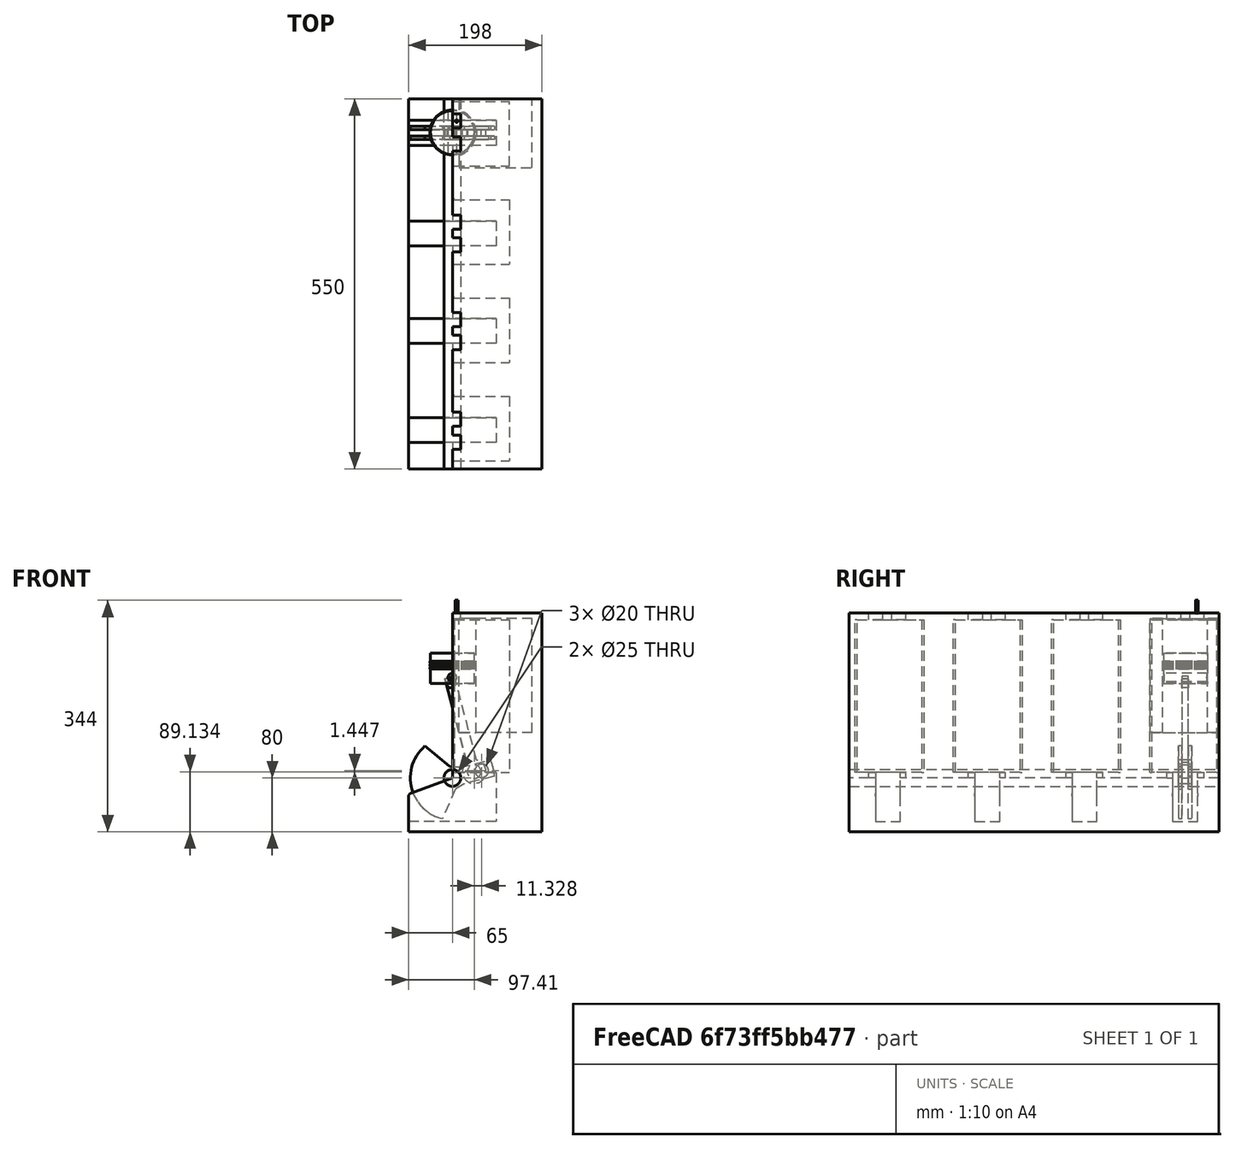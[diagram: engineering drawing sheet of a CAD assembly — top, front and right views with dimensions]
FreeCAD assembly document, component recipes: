
FREECAD ASSEMBLY — COMPONENT RECIPES ("motor")

This assembly document has 7 components, labeled P0..P6 below (a component is one placed body or linked part). 7 of them carry a construction recipe — the FreeCAD feature program that regenerates the part from scratch, quoted from this document or its linked companion documents; the rest are supplied as boundary geometry only. No exploded tour is included for this assembly.
COMPONENT P0 — recipe-attached ("Body", modeled in this document).
Construction recipe (the document's own serialized feature program — sketch geometry with constraints, then the solid features built on it; lengths are millimeters unless a unit is written):

FEATURE [Sketcher::SketchObject] Sketch
  ArcFitTolerance = 1e-06
  AttachmentSupport = -> [XZ_Plane]
  FullyConstrained = true
  MakeInternals = false
  MapMode = 5
  Placement = pos=(0,0,0) rot=(1,0,0;1.5708rad)
  sketch-geometry (1):
    g0: Circle CenterX=0 CenterY=0 CenterZ=0 NormalX=0 NormalY=0 NormalZ=1 AngleXU=0 Radius=12.5
  constraints (2):
    c: Diameter(g0) = 25
    c: Coincident(g0,g-1)
FEATURE [PartDesign::Pad] Pad
  Direction = (0,-1,2e-16)
  Length = 550
  Length2 = 10
  Placement = pos=(0,0,0) rot=(1,0,0;1.5708rad)
  Profile = -> Sketch
  ReferenceAxis = -> Sketch [N_Axis]
  Refine = true
  Suppressed = false
  Type = 0
FEATURE [PartDesign::Body] Body
  AllowCompound = false
  Group = -> [Sketch,Pad]
  Origin = -> Origin
  Placement = pos=(0,43,0) rot=(0,0,1;0rad)
  Tip = -> Pad
COMPONENT P1 — recipe-attached ("Rotor", modeled in this document).
Construction recipe (the document's own serialized feature program — sketch geometry with constraints, then the solid features built on it; lengths are millimeters unless a unit is written):

FEATURE [Sketcher::SketchObject] Sketch001
  ArcFitTolerance = 1e-06
  AttachmentSupport = -> [XZ_Plane001]
  FullyConstrained = true
  MakeInternals = false
  MapMode = 5
  Placement = pos=(0,0,0) rot=(1,0,0;1.5708rad)
  sketch-geometry (1):
    g0: Circle CenterX=0 CenterY=0 CenterZ=0 NormalX=0 NormalY=0 NormalZ=1 AngleXU=0 Radius=62.5
  constraints (2):
    c: Diameter(g0) = 125
    c: Coincident(g0,g-1)
FEATURE [PartDesign::Pad] Pad001
  Direction = (0,-1,2e-16)
  Length = 20
  Length2 = 10
  Placement = pos=(0,0,0) rot=(1,0,0;1.5708rad)
  Profile = -> Sketch001
  ReferenceAxis = -> Sketch001 [N_Axis]
  Refine = true
  Suppressed = false
  Type = 0
FEATURE [Sketcher::SketchObject] Sketch008
  ArcFitTolerance = 1e-06
  AttachmentSupport = -> [YZ_Plane001]
  FullyConstrained = false
  MakeInternals = false
  MapMode = 5
  Placement = pos=(0,0,0) rot=(0.57735,0.57735,0.57735;2.0944rad)
  sketch-geometry (4):
    g0: LineSegment StartX=-14.5 StartY=72.9316 StartZ=0 EndX=-14.5 EndY=-69.5294 EndZ=0
    g1: LineSegment StartX=-14.5 StartY=-69.5294 StartZ=0 EndX=-5.5 EndY=-69.5294 EndZ=0
    g2: LineSegment StartX=-5.5 StartY=-69.5294 StartZ=0 EndX=-5.5 EndY=72.9316 EndZ=0
    g3: LineSegment StartX=-5.5 StartY=72.9316 StartZ=0 EndX=-14.5 EndY=72.9316 EndZ=0
  constraints (10):
    c: Coincident(g0,g1)
    c: Coincident(g1,g2)
    c: Coincident(g2,g3)
    c: Coincident(g3,g0)
    c: Vertical(g0)
    c: Vertical(g2)
    c: Horizontal(g1)
    c: Horizontal(g3)
    c: DistanceX(g2,g-1) = 5.5
    c: DistanceX(g0,g-1) = 14.5
FEATURE [Sketcher::SketchObject] Sketch009
  ArcFitTolerance = 1e-06
  AttachmentSupport = -> [XZ_Plane001]
  FullyConstrained = true
  MakeInternals = false
  MapMode = 5
  Placement = pos=(0,0,0) rot=(1,0,0;1.5708rad)
  sketch-geometry (1):
    g0: Circle CenterX=0 CenterY=45 CenterZ=0 NormalX=0 NormalY=0 NormalZ=1 AngleXU=0 Radius=10
  constraints (3):
    c: Diameter(g0) = 20
    c: PointOnObject(g0,g-2)
    c: Distance(g0,g-1) = 45
FEATURE [Sketcher::SketchObject] Sketch002
  ArcFitTolerance = 1e-06
  AttachmentSupport = -> [XZ_Plane001]
  FullyConstrained = true
  MakeInternals = false
  MapMode = 5
  Placement = pos=(0,0,0) rot=(1,0,0;1.5708rad)
  sketch-geometry (1):
    g0: Circle CenterX=0 CenterY=0 CenterZ=0 NormalX=0 NormalY=0 NormalZ=1 AngleXU=0 Radius=12.5
  constraints (2):
    c: Diameter(g0) = 25
    c: Coincident(g0,g-1)
FEATURE [PartDesign::Pocket] Pocket
  BaseFeature = -> Pad001
  Direction = (0,1,-2e-16)
  Length = 200
  Length2 = 5
  Midplane = true
  Placement = pos=(0,0,0) rot=(1,0,0;1.5708rad)
  Profile = -> Sketch002
  ReferenceAxis = -> Sketch002 [N_Axis]
  Refine = true
  Suppressed = false
  Type = 1
FEATURE [Sketcher::SketchObject] Sketch003
  ArcFitTolerance = 1e-06
  AttachmentSupport = -> [XZ_Plane001]
  ExternalGeometry = -> [Pocket]
  FullyConstrained = false
  MakeInternals = false
  MapMode = 5
  Placement = pos=(0,0,0) rot=(1,0,0;1.5708rad)
  sketch-geometry (15):
    g0: LineSegment StartX=-17.5 StartY=0 StartZ=0 EndX=-55.6237 EndY=-28.5 EndZ=0
    g1: LineSegment StartX=17.5 StartY=0 StartZ=0 EndX=55.6237 EndY=-28.5 EndZ=0
    g2: LineSegment StartX=-12.5 StartY=15 StartZ=0 EndX=-12.5 EndY=61.2372 EndZ=0
    g3: LineSegment StartX=12.5 StartY=61.2372 StartZ=0 EndX=12.5 EndY=15 EndZ=0
    g4: LineSegment StartX=-17.5 StartY=0 StartZ=0 EndX=-12.5 EndY=15 EndZ=0
    g5: LineSegment StartX=12.5 StartY=15 StartZ=0 EndX=17.5 EndY=0 EndZ=0
    g6: LineSegment StartX=-12.5 StartY=61.2372 StartZ=0 EndX=-10.2152 EndY=69.9879 EndZ=0
    g7: LineSegment StartX=12.5 StartY=61.2372 StartZ=0 EndX=12.4683 EndY=71.345 EndZ=0
    g8: LineSegment StartX=-55.6237 StartY=-28.5 StartZ=0 EndX=-118.404 EndY=45.7859 EndZ=0
    g9: LineSegment StartX=-118.404 StartY=45.7859 StartZ=0 EndX=-16.6365 EndY=95.2543 EndZ=0
    g10: LineSegment StartX=-16.6365 StartY=95.2543 StartZ=0 EndX=53.285 EndY=95.2543 EndZ=0
    g11: LineSegment StartX=53.285 StartY=95.2543 StartZ=0 EndX=87.1096 EndY=0 EndZ=0
    g12: LineSegment StartX=87.1096 StartY=0 StartZ=0 EndX=60.5266 EndY=-36.2011 EndZ=0
    g13: LineSegment StartX=60.5266 StartY=-36.2011 StartZ=0 EndX=55.6237 EndY=-28.5 EndZ=0
    g14: LineSegment StartX=-10.2152 StartY=69.9879 StartZ=0 EndX=12.4683 EndY=71.345 EndZ=0
  constraints (30):
    c: PointOnObject(g0,g-1)
    c: PointOnObject(g1,g-3)
    c: Symmetric(g0,g1,g-2)
    c: DistanceX(g-1,g1) = 17.5
    c: DistanceY(g1,g-1) = 28.5
    c: Symmetric(g0,g1,g-2)
    c: Vertical(g2)
    c: PointOnObject(g3,g-3)
    c: Vertical(g3)
    c: DistanceX(g2,g-1) = 12.5
    c: Symmetric(g2,g3,g-2)
    c: Horizontal(g2,g3)
    c: DistanceY(g-1,g2) = 15
    c: Coincident(g4,g2)
    c: Coincident(g5,g3)
    c: Coincident(g4,g0)
    c: Coincident(g5,g1)
    c: Coincident(g6,g2)
    c: Coincident(g7,g3)
    c: Coincident(g0,g8)
    c: Coincident(g8,g9)
    c: Coincident(g9,g10)
    c: Horizontal(g10)
    c: Coincident(g10,g11)
    c: PointOnObject(g11,g-1)
    c: Coincident(g11,g12)
    c: Coincident(g13,g12)
    c: Coincident(g13,g1)
    c: Coincident(g14,g6)
    c: Coincident(g14,g7)
FEATURE [PartDesign::Pocket] Pocket001
  BaseFeature = -> Pocket
  Direction = (0,1,-2e-16)
  Length = 5
  Length2 = 5
  Placement = pos=(0,0,0) rot=(1,0,0;1.5708rad)
  Profile = -> Sketch003
  ReferenceAxis = -> Sketch003 [N_Axis]
  Refine = true
  Reversed = true
  Suppressed = false
  Type = 1
FEATURE [PartDesign::Pocket] Pocket004
  BaseFeature = -> Pocket001
  Direction = (-1,0,0)
  Length = 5
  Length2 = 5
  Midplane = true
  Placement = pos=(0,0,0) rot=(1,0,0;1.5708rad)
  Profile = -> Sketch008
  ReferenceAxis = -> Sketch008 [N_Axis]
  Refine = true
  Suppressed = false
  Type = 1
FEATURE [PartDesign::Pocket] Pocket005
  BaseFeature = -> Pocket004
  Direction = (0,1,-2e-16)
  Length = 5
  Length2 = 5
  Midplane = true
  Placement = pos=(0,0,0) rot=(1,0,0;1.5708rad)
  Profile = -> Sketch009
  ReferenceAxis = -> Sketch009 [N_Axis]
  Refine = true
  Suppressed = false
  Type = 1
FEATURE [PartDesign::Pocket] Pocket013
  BaseFeature = -> Pocket005
  Direction = (-1,0,0)
  Length = 5
  Length2 = 5
  Placement = pos=(0,0,0) rot=(1,0,0;1.5708rad)
  Profile = -> Sketch008
  ReferenceAxis = -> Sketch008 [N_Axis]
  Refine = true
  Suppressed = false
  Type = 0
FEATURE [PartDesign::Body] Body001  label="Rotor"
  AllowCompound = true
  Group = -> [Sketch001,Pad001,Sketch002,Pocket,Sketch003,Pocket001,Sketch008,Pocket004,Sketch009,Pocket005,Pocket013]
  Origin = -> Origin001
  Placement = pos=(0,2.5,0) rot=(0,-1,0;-1.33343rad)
  Tip = -> Pocket013
COMPONENT P2 — recipe-attached ("Bar", modeled in this document).
Construction recipe (the document's own serialized feature program — sketch geometry with constraints, then the solid features built on it; lengths are millimeters unless a unit is written):

FEATURE [Sketcher::SketchObject] Sketch004
  ArcFitTolerance = 1e-06
  AttachmentSupport = -> [XZ_Plane002]
  FullyConstrained = true
  MakeInternals = false
  MapMode = 5
  Placement = pos=(0,0,0) rot=(1,0,0;1.5708rad)
  sketch-geometry (1):
    g0: Circle CenterX=0 CenterY=45 CenterZ=0 NormalX=0 NormalY=0 NormalZ=1 AngleXU=0 Radius=17.5
  constraints (3):
    c: Diameter(g0) = 35
    c: PointOnObject(g0,g-2)
    c: DistanceY(g-1,g0) = 45
FEATURE [PartDesign::Pad] Pad002
  Direction = (0,-1,2e-16)
  Length = 15
  Length2 = 10
  Placement = pos=(0,0,0) rot=(1,0,0;1.5708rad)
  Profile = -> Sketch004
  ReferenceAxis = -> Sketch004 [N_Axis]
  Refine = true
  Suppressed = false
  Type = 0
  UseCustomVector = true
FEATURE [Sketcher::SketchObject] Sketch005
  ArcFitTolerance = 1e-06
  AttachmentSupport = -> [Pad002]
  ExternalGeometry = -> [Pad002]
  FullyConstrained = true
  MakeInternals = false
  MapMode = 5
  Placement = pos=(0,1e-14,0) rot=(-1,0,0;1.5708rad)
  sketch-geometry (4):
    g0: LineSegment StartX=-7.5 StartY=-60.8114 StartZ=0 EndX=-7.5 EndY=-190 EndZ=0
    g1: LineSegment StartX=7.5 StartY=-60.8114 StartZ=0 EndX=7.5 EndY=-190 EndZ=0
    g2: LineSegment StartX=-7.5 StartY=-190 StartZ=0 EndX=7.5 EndY=-190 EndZ=0
    g3: LineSegment StartX=-7.5 StartY=-60.8114 StartZ=0 EndX=7.5 EndY=-60.8114 EndZ=0
  constraints (11):
    c: PointOnObject(g0,g-3)
    c: Vertical(g0)
    c: PointOnObject(g1,g-3)
    c: Vertical(g1)
    c: Symmetric(g1,g0,g-2)
    c: DistanceX(g-1,g1) = 7.5
    c: Coincident(g2,g0)
    c: Coincident(g2,g1)
    c: DistanceY(g1,g-1) = 190
    c: Coincident(g3,g0)
    c: Coincident(g3,g1)
FEATURE [PartDesign::Pad] Pad004
  BaseFeature = -> Pad002
  Direction = (0,1,2e-16)
  Length = 15
  Length2 = 10
  Placement = pos=(0,0,0) rot=(1,0,0;1.5708rad)
  Profile = -> Sketch005
  ReferenceAxis = -> Sketch005 [N_Axis]
  Refine = true
  Reversed = true
  Suppressed = false
  Type = 0
FEATURE [Sketcher::SketchObject] Sketch006
  ArcFitTolerance = 1e-06
  AttachmentSupport = -> [XZ_Plane002]
  FullyConstrained = true
  MakeInternals = false
  MapMode = 5
  Placement = pos=(0,0,0) rot=(1,0,0;1.5708rad)
  sketch-geometry (1):
    g0: Circle CenterX=0 CenterY=45 CenterZ=0 NormalX=0 NormalY=0 NormalZ=1 AngleXU=0 Radius=10
  constraints (3):
    c: Diameter(g0) = 20
    c: PointOnObject(g0,g-2)
    c: DistanceY(g-1,g0) = 45
FEATURE [PartDesign::Pocket] Pocket002
  BaseFeature = -> Pad004
  Direction = (0,1,-2e-16)
  Length = 10
  Length2 = 5
  Midplane = true
  Placement = pos=(0,0,0) rot=(1,0,0;1.5708rad)
  Profile = -> Sketch006
  ReferenceAxis = -> Sketch006 [N_Axis]
  Refine = true
  Suppressed = false
  Type = 1
FEATURE [Sketcher::SketchObject] Sketch007
  ArcFitTolerance = 1e-06
  AttachmentSupport = -> [YZ_Plane002]
  FullyConstrained = false
  MakeInternals = false
  MapMode = 5
  Placement = pos=(0,0,0) rot=(0.57735,0.57735,0.57735;2.0944rad)
  sketch-geometry (8):
    g0: LineSegment StartX=-3 StartY=190.161 StartZ=0 EndX=-3 EndY=21.3692 EndZ=0
    g1: LineSegment StartX=-12 StartY=21.3692 StartZ=0 EndX=-12 EndY=191.131 EndZ=0
    g2: LineSegment StartX=-3 StartY=21.3692 StartZ=0 EndX=24.874 EndY=21.3692 EndZ=0
    g3: LineSegment StartX=24.874 StartY=21.3692 StartZ=0 EndX=24.874 EndY=192.767 EndZ=0
    g4: LineSegment StartX=-12 StartY=21.3692 StartZ=0 EndX=-43.0832 EndY=21.3692 EndZ=0
    g5: LineSegment StartX=-43.0832 StartY=21.3692 StartZ=0 EndX=-43.0832 EndY=191.395 EndZ=0
    g6: LineSegment StartX=-43.0832 StartY=191.395 StartZ=0 EndX=24.874 EndY=192.767 EndZ=0
    g7: LineSegment StartX=-12 StartY=191.131 StartZ=0 EndX=-3 EndY=190.161 EndZ=0
  constraints (16):
    c: Vertical(g0)
    c: DistanceX(g0,g-1) = 3
    c: Vertical(g1)
    c: DistanceX(g1,g-1) = 12
    c: Coincident(g2,g0)
    c: Horizontal(g2)
    c: Coincident(g3,g2)
    c: Vertical(g3)
    c: Coincident(g4,g1)
    c: Horizontal(g4)
    c: Coincident(g5,g4)
    c: Vertical(g5)
    c: Coincident(g6,g5)
    c: Coincident(g6,g3)
    c: Coincident(g7,g1)
    c: Coincident(g7,g0)
FEATURE [PartDesign::Pocket] Pocket003
  BaseFeature = -> Pocket002
  Direction = (-1,0,0)
  Length = 5
  Length2 = 5
  Midplane = true
  Placement = pos=(0,0,0) rot=(1,0,0;1.5708rad)
  Profile = -> Sketch007
  ReferenceAxis = -> Sketch007 [N_Axis]
  Refine = true
  Suppressed = false
  Type = 1
FEATURE [Sketcher::SketchObject] Sketch012
  ArcFitTolerance = 1e-06
  AttachmentSupport = -> [XZ_Plane002]
  FullyConstrained = true
  MakeInternals = false
  MapMode = 5
  Placement = pos=(0,0,0) rot=(1,0,0;1.5708rad)
  sketch-geometry (1):
    g0: Circle CenterX=0 CenterY=180.5 CenterZ=0 NormalX=0 NormalY=0 NormalZ=1 AngleXU=0 Radius=6.5
  constraints (3):
    c: Diameter(g0) = 13
    c: PointOnObject(g0,g-2)
    c: Distance(g0,g-1) = 180.5
FEATURE [PartDesign::Pocket] Pocket007
  BaseFeature = -> Pocket003
  Direction = (0,1,-2e-16)
  Length = 5
  Length2 = 5
  Midplane = true
  Placement = pos=(0,0,0) rot=(1,0,0;1.5708rad)
  Profile = -> Sketch012
  ReferenceAxis = -> Sketch012 [N_Axis]
  Refine = true
  Suppressed = false
  Type = 1
FEATURE [PartDesign::Body] Body002  label="Bar"
  AllowCompound = false
  Group = -> [Sketch004,Pad002,Sketch005,Pad004,Sketch006,Pocket002,Sketch007,Pocket003,Sketch012,Pocket007]
  Origin = -> Origin002
  Placement = pos=(43.7378,0,-34.4169) rot=(0,1,0;-0.254456rad)
  Tip = -> Pocket007
COMPONENT P3 — recipe-attached ("PistonHead", modeled in this document).
Construction recipe (the document's own serialized feature program — sketch geometry with constraints, then the solid features built on it; lengths are millimeters unless a unit is written):

FEATURE [Sketcher::SketchObject] Sketch010
  ArcFitTolerance = 1e-06
  AttachmentSupport = -> [XY_Plane003]
  FullyConstrained = true
  MakeInternals = false
  MapMode = 5
  sketch-geometry (1):
    g0: Circle CenterX=0 CenterY=0 CenterZ=0 NormalX=0 NormalY=0 NormalZ=1 AngleXU=0 Radius=32.5
  constraints (2):
    c: Diameter(g0) = 65
    c: Coincident(g0,g-1)
FEATURE [PartDesign::Pad] Pad005
  Direction = (0,0,1)
  Length = 45
  Length2 = 10
  Profile = -> Sketch010
  ReferenceAxis = -> Sketch010 [N_Axis]
  Refine = true
  Suppressed = false
  Type = 0
FEATURE [Sketcher::SketchObject] Sketch011
  ArcFitTolerance = 1e-06
  AttachmentSupport = -> [XZ_Plane003]
  FullyConstrained = true
  MakeInternals = false
  MapMode = 5
  Placement = pos=(0,0,0) rot=(1,0,0;1.5708rad)
  sketch-geometry (1):
    g0: Circle CenterX=0 CenterY=8.5 CenterZ=0 NormalX=0 NormalY=0 NormalZ=1 AngleXU=0 Radius=6.5
  constraints (3):
    c: Diameter(g0) = 13
    c: PointOnObject(g0,g-2)
    c: DistanceY(g-1,g0) = 8.5
FEATURE [PartDesign::Pocket] Pocket006
  BaseFeature = -> Pad005
  Direction = (0,1,-2e-16)
  Length = 5
  Length2 = 5
  Midplane = true
  Profile = -> Sketch011
  ReferenceAxis = -> Sketch011 [N_Axis]
  Refine = true
  Suppressed = false
  Type = 1
FEATURE [Sketcher::SketchObject] Sketch013
  ArcFitTolerance = 1e-06
  AttachmentSupport = -> [XZ_Plane003]
  ExternalGeometry = -> [Pocket006]
  FullyConstrained = false
  MakeInternals = false
  MapMode = 5
  Placement = pos=(0,0,0) rot=(1,0,0;1.5708rad)
  sketch-geometry (12):
    g0: LineSegment StartX=32.492 StartY=21.5654 StartZ=0 EndX=33.5 EndY=21.5654 EndZ=0
    g1: LineSegment StartX=33.5 StartY=21.5654 StartZ=0 EndX=33.5 EndY=23.7725 EndZ=0
    g2: LineSegment StartX=33.5 StartY=23.7725 StartZ=0 EndX=32.4874 EndY=23.7725 EndZ=0
    g3: LineSegment StartX=32.5 StartY=26 StartZ=0 EndX=33.5 EndY=26 EndZ=0
    g4: LineSegment StartX=33.5 StartY=26 StartZ=0 EndX=33.5 EndY=28.2071 EndZ=0
    g5: LineSegment StartX=33.5 StartY=28.2071 StartZ=0 EndX=32.5 EndY=28.2071 EndZ=0
    g6: LineSegment StartX=32.5 StartY=28.2071 StartZ=0 EndX=32.5 EndY=26 EndZ=0
    g7: LineSegment StartX=32.5 StartY=32.6267 StartZ=0 EndX=32.5 EndY=30.4196 EndZ=0
    g8: LineSegment StartX=32.5 StartY=30.4196 StartZ=0 EndX=33.5 EndY=30.4196 EndZ=0
    g9: LineSegment StartX=33.5 StartY=30.4196 StartZ=0 EndX=33.5 EndY=32.6267 EndZ=0
    g10: LineSegment StartX=33.5 StartY=32.6267 StartZ=0 EndX=32.5 EndY=32.6267 EndZ=0
    g11: LineSegment StartX=32.4874 StartY=23.7725 StartZ=0 EndX=32.492 EndY=21.5654 EndZ=0
  constraints (31):
    c: Horizontal(g0)
    c: Horizontal(g2)
    c: DistanceX(g-1,g1) = 33.5
    c: Coincident(g3,g4)
    c: Coincident(g4,g5)
    c: Coincident(g5,g6)
    c: Coincident(g6,g3)
    c: Horizontal(g3)
    c: Horizontal(g5)
    c: Vertical(g4)
    c: Vertical(g6)
    c: PointOnObject(g3,g-3)
    c: DistanceX(g-1,g4) = 33.5
    c: DistanceY(g-1,g3) = 26
    c: Vertical(g0,g1)
    c: Coincident(g7,g8)
    c: Coincident(g8,g9)
    c: Coincident(g9,g10)
    c: Coincident(g10,g7)
    c: Vertical(g7)
    c: Vertical(g9)
    c: Horizontal(g8)
    c: Horizontal(g10)
    c: PointOnObject(g7,g-3)
    c: Equal(g9,g4)
    c: Equal(g1,g4)
    c: DistanceX(g-1,g9) = 33.5
    c: Coincident(g1,g0)
    c: Coincident(g1,g2)
    c: Coincident(g11,g2)
    c: Coincident(g11,g0)
FEATURE [PartDesign::Revolution] Revolution
  Angle = 360
  Angle2 = 60
  Axis = (0,2e-16,1)
  Base = (0,0,0)
  BaseFeature = -> Pocket006
  Profile = -> Sketch013
  ReferenceAxis = -> Sketch013 [V_Axis]
  Refine = true
  Reversed = true
  Suppressed = false
  Type = 0
FEATURE [PartDesign::Body] Body003  label="PistonHead"
  AllowCompound = false
  Group = -> [Sketch010,Pad005,Sketch011,Pocket006,Sketch013,Revolution]
  Origin = -> Origin003
  Placement = pos=(0,-7,140.58) rot=(0,0,1;0rad)
  Tip = -> Revolution
COMPONENT P4 — recipe-attached ("Case", modeled in this document).
Construction recipe (the document's own serialized feature program — sketch geometry with constraints, then the solid features built on it; lengths are millimeters unless a unit is written):

FEATURE [Sketcher::SketchObject] Sketch014
  ArcFitTolerance = 1e-06
  AttachmentSupport = -> [XZ_Plane004]
  FullyConstrained = true
  MakeInternals = false
  MapMode = 5
  Placement = pos=(0,0,0) rot=(1,0,0;1.5708rad)
  sketch-geometry (6):
    g0: LineSegment StartX=0 StartY=245 StartZ=0 EndX=0 EndY=0 EndZ=0
    g1: LineSegment StartX=0 StartY=0 StartZ=0 EndX=-65 EndY=-24 EndZ=0
    g2: LineSegment StartX=-65 StartY=-24 StartZ=0 EndX=-65 EndY=-80 EndZ=0
    g3: LineSegment StartX=-65 StartY=-80 StartZ=0 EndX=133 EndY=-80 EndZ=0
    g4: LineSegment StartX=133 StartY=-80 StartZ=0 EndX=133 EndY=245 EndZ=0
    g5: LineSegment StartX=133 StartY=245 StartZ=0 EndX=0 EndY=245 EndZ=0
  constraints (17):
    c: Coincident(g0,g-1)
    c: Vertical(g0)
    c: Coincident(g0,g1)
    c: Coincident(g1,g2)
    c: Vertical(g2)
    c: Coincident(g2,g3)
    c: Horizontal(g3)
    c: Coincident(g3,g4)
    c: Vertical(g4)
    c: Coincident(g4,g5)
    c: Coincident(g5,g0)
    c: Horizontal(g4,g0)
    c: DistanceY(g-1,g4) = 245
    c: DistanceY(g1,g-1) = 24
    c: DistanceY(g2,g-1) = 80
    c: DistanceX(g-1,g3) = 133
    c: DistanceX(g1,g-1) = 65
FEATURE [PartDesign::Pad] Pad006
  Direction = (0,-1,2e-16)
  Length = 550
  Length2 = 10
  Placement = pos=(0,0,0) rot=(1,0,0;1.5708rad)
  Profile = -> Sketch014
  ReferenceAxis = -> Sketch014 [N_Axis]
  Refine = true
  Suppressed = false
  Type = 0
FEATURE [Sketcher::SketchObject] Sketch015
  ArcFitTolerance = 1e-06
  AttachmentSupport = -> [Pad006]
  FullyConstrained = true
  MakeInternals = false
  MapMode = 5
  Placement = pos=(0,0,0) rot=(0.707107,0,-0.707107;3.14159rad)
  sketch-geometry (16):
    g0: LineSegment StartX=-235 StartY=4 StartZ=0 EndX=-8 EndY=4 EndZ=0
    g1: LineSegment StartX=-8 StartY=4 StartZ=0 EndX=-8 EndY=100 EndZ=0
    g2: LineSegment StartX=-8 StartY=100 StartZ=0 EndX=-235 EndY=100 EndZ=0
    g3: LineSegment StartX=-235 StartY=100 StartZ=0 EndX=-235 EndY=4 EndZ=0
    g4: LineSegment StartX=-235 StartY=150 StartZ=0 EndX=-8 EndY=150 EndZ=0
    g5: LineSegment StartX=-8 StartY=150 StartZ=0 EndX=-8 EndY=246 EndZ=0
    g6: LineSegment StartX=-8 StartY=246 StartZ=0 EndX=-235 EndY=246 EndZ=0
    g7: LineSegment StartX=-235 StartY=246 StartZ=0 EndX=-235 EndY=150 EndZ=0
    g8: LineSegment StartX=-235 StartY=296 StartZ=0 EndX=-8 EndY=296 EndZ=0
    g9: LineSegment StartX=-8 StartY=296 StartZ=0 EndX=-8 EndY=392 EndZ=0
    g10: LineSegment StartX=-8 StartY=392 StartZ=0 EndX=-235 EndY=392 EndZ=0
    g11: LineSegment StartX=-235 StartY=392 StartZ=0 EndX=-235 EndY=296 EndZ=0
    g12: LineSegment StartX=-235 StartY=442 StartZ=0 EndX=-8 EndY=442 EndZ=0
    g13: LineSegment StartX=-8 StartY=442 StartZ=0 EndX=-8 EndY=538 EndZ=0
    g14: LineSegment StartX=-8 StartY=538 StartZ=0 EndX=-235 EndY=538 EndZ=0
    g15: LineSegment StartX=-235 StartY=538 StartZ=0 EndX=-235 EndY=442 EndZ=0
  constraints (48):
    c: Coincident(g0,g1)
    c: Coincident(g1,g2)
    c: Coincident(g2,g3)
    c: Coincident(g3,g0)
    c: Horizontal(g0)
    c: Horizontal(g2)
    c: Vertical(g1)
    c: Vertical(g3)
    c: Coincident(g4,g5)
    c: Coincident(g5,g6)
    c: Coincident(g6,g7)
    c: Coincident(g7,g4)
    c: Horizontal(g4)
    c: Horizontal(g6)
    c: Vertical(g5)
    c: Vertical(g7)
    c: Coincident(g8,g9)
    c: Coincident(g9,g10)
    c: Coincident(g10,g11)
    c: Coincident(g11,g8)
    c: Horizontal(g8)
    c: Horizontal(g10)
    c: Vertical(g9)
    c: Vertical(g11)
    c: Coincident(g12,g13)
    c: Coincident(g13,g14)
    c: Coincident(g14,g15)
    c: Coincident(g15,g12)
    c: Horizontal(g12)
    c: Horizontal(g14)
    c: Vertical(g13)
    c: Vertical(g15)
    c: DistanceX(g0,g-1) = 8
    c: DistanceX(g0,g-1) = 235
    c: DistanceY(g-1,g2) = 100
    c: DistanceY(g-1,g0) = 4
    c: Equal(g3,g7)
    c: Equal(g7,g11)
    c: Equal(g11,g15)
    c: Equal(g2,g4)
    c: Equal(g4,g8)
    c: Equal(g8,g12)
    c: Vertical(g1,g4)
    c: Vertical(g4,g8)
    c: Vertical(g8,g12)
    c: DistanceY(g1,g4) = 50
    c: DistanceY(g5,g8) = 50
    c: DistanceY(g9,g12) = 50
FEATURE [PartDesign::Pocket] Pocket008
  BaseFeature = -> Pad006
  Direction = (1,0,2e-16)
  Length = 85
  Length2 = 5
  Placement = pos=(0,0,0) rot=(1,0,0;1.5708rad)
  Profile = -> Sketch015
  ReferenceAxis = -> Sketch015 [N_Axis]
  Refine = true
  Suppressed = false
  Type = 0
FEATURE [Sketcher::SketchObject] Sketch016
  ArcFitTolerance = 1e-06
  AttachmentSupport = -> [YZ_Plane004]
  FullyConstrained = false
  MakeInternals = false
  MapMode = 5
  Placement = pos=(0,0,0) rot=(0.57735,0.57735,0.57735;2.0944rad)
  sketch-geometry (16):
    g0: LineSegment StartX=-32 StartY=75 StartZ=0 EndX=-69 EndY=75 EndZ=0
    g1: LineSegment StartX=-69 StartY=75 StartZ=0 EndX=-69 EndY=-65 EndZ=0
    g2: LineSegment StartX=-69 StartY=-65 StartZ=0 EndX=-32 EndY=-65 EndZ=0
    g3: LineSegment StartX=-32 StartY=-65 StartZ=0 EndX=-32 EndY=75 EndZ=0
    g4: LineSegment StartX=-181.411 StartY=75 StartZ=0 EndX=-218.411 EndY=75 EndZ=0
    g5: LineSegment StartX=-218.411 StartY=75 StartZ=0 EndX=-218.411 EndY=-65 EndZ=0
    g6: LineSegment StartX=-218.411 StartY=-65 StartZ=0 EndX=-181.411 EndY=-65 EndZ=0
    g7: LineSegment StartX=-181.411 StartY=-65 StartZ=0 EndX=-181.411 EndY=75 EndZ=0
    g8: LineSegment StartX=-326.116 StartY=75 StartZ=0 EndX=-363.116 EndY=75 EndZ=0
    g9: LineSegment StartX=-363.116 StartY=75 StartZ=0 EndX=-363.116 EndY=-65 EndZ=0
    g10: LineSegment StartX=-363.116 StartY=-65 StartZ=0 EndX=-326.116 EndY=-65 EndZ=0
    g11: LineSegment StartX=-326.116 StartY=-65 StartZ=0 EndX=-326.116 EndY=75 EndZ=0
    g12: LineSegment StartX=-473.828 StartY=75 StartZ=0 EndX=-510.828 EndY=75 EndZ=0
    g13: LineSegment StartX=-510.828 StartY=75 StartZ=0 EndX=-510.828 EndY=-65 EndZ=0
    g14: LineSegment StartX=-510.828 StartY=-65 StartZ=0 EndX=-473.828 EndY=-65 EndZ=0
    g15: LineSegment StartX=-473.828 StartY=-65 StartZ=0 EndX=-473.828 EndY=75 EndZ=0
  constraints (45):
    c: Coincident(g0,g1)
    c: Coincident(g1,g2)
    c: Coincident(g2,g3)
    c: Coincident(g3,g0)
    c: Horizontal(g0)
    c: Horizontal(g2)
    c: Vertical(g1)
    c: Vertical(g3)
    c: Coincident(g4,g5)
    c: Coincident(g5,g6)
    c: Coincident(g6,g7)
    c: Coincident(g7,g4)
    c: Horizontal(g4)
    c: Horizontal(g6)
    c: Vertical(g5)
    c: Vertical(g7)
    c: Coincident(g8,g9)
    c: Coincident(g9,g10)
    c: Coincident(g10,g11)
    c: Coincident(g11,g8)
    c: Horizontal(g8)
    c: Horizontal(g10)
    c: Vertical(g9)
    c: Vertical(g11)
    c: Coincident(g12,g13)
    c: Coincident(g13,g14)
    c: Coincident(g14,g15)
    c: Coincident(g15,g12)
    c: Horizontal(g12)
    c: Horizontal(g14)
    c: Vertical(g13)
    c: Vertical(g15)
    c: DistanceX(g2,g-1) = 32
    c: DistanceX(g1,g-1) = 69
    c: Equal(g2,g6)
    c: Equal(g6,g10)
    c: Equal(g10,g14)
    c: DistanceY(g-1,g0) = 75
    c: Equal(g3,g7)
    c: Equal(g7,g11)
    c: Equal(g11,g15)
    c: DistanceY(g2,g-1) = 65
    c: Horizontal(g0,g4)
    c: Horizontal(g4,g8)
    c: Horizontal(g8,g12)
FEATURE [PartDesign::Pocket] Pocket009
  BaseFeature = -> Pocket008
  Direction = (-1,0,0)
  Length = 130
  Length2 = 5
  Midplane = true
  Placement = pos=(0,0,0) rot=(1,0,0;1.5708rad)
  Profile = -> Sketch016
  ReferenceAxis = -> Sketch016 [N_Axis]
  Refine = true
  Suppressed = false
  Type = 0
FEATURE [Sketcher::SketchObject] Sketch019
  ArcFitTolerance = 1e-06
  AttachmentSupport = -> [XY_Plane004]
  ExternalGeometry = -> [Pocket009]
  FullyConstrained = true
  MakeInternals = false
  MapMode = 5
  sketch-geometry (32):
    g0: LineSegment StartX=0 StartY=-22.5 StartZ=0 EndX=0 EndY=-43.5 EndZ=0
    g1: LineSegment StartX=0 StartY=-43.5 StartZ=0 EndX=12.5 EndY=-43.5 EndZ=0
    g2: LineSegment StartX=12.5 StartY=-43.5 StartZ=0 EndX=12.5 EndY=-22.5 EndZ=0
    g3: LineSegment StartX=12.5 StartY=-22.5 StartZ=0 EndX=0 EndY=-22.5 EndZ=0
    g4: LineSegment StartX=0 StartY=-56.5 StartZ=0 EndX=0 EndY=-77.5 EndZ=0
    g5: LineSegment StartX=0 StartY=-77.5 StartZ=0 EndX=12.5 EndY=-77.5 EndZ=0
    g6: LineSegment StartX=12.5 StartY=-77.5 StartZ=0 EndX=12.5 EndY=-56.5 EndZ=0
    g7: LineSegment StartX=12.5 StartY=-56.5 StartZ=0 EndX=0 EndY=-56.5 EndZ=0
    g8: LineSegment StartX=0 StartY=-172.5 StartZ=0 EndX=0 EndY=-193.5 EndZ=0
    g9: LineSegment StartX=0 StartY=-193.5 StartZ=0 EndX=12.5 EndY=-193.5 EndZ=0
    g10: LineSegment StartX=12.5 StartY=-193.5 StartZ=0 EndX=12.5 EndY=-172.5 EndZ=0
    g11: LineSegment StartX=12.5 StartY=-172.5 StartZ=0 EndX=0 EndY=-172.5 EndZ=0
    g12: LineSegment StartX=0 StartY=-206.5 StartZ=0 EndX=0 EndY=-227.5 EndZ=0
    g13: LineSegment StartX=0 StartY=-227.5 StartZ=0 EndX=12.5 EndY=-227.5 EndZ=0
    g14: LineSegment StartX=12.5 StartY=-227.5 StartZ=0 EndX=12.5 EndY=-206.5 EndZ=0
    g15: LineSegment StartX=12.5 StartY=-206.5 StartZ=0 EndX=0 EndY=-206.5 EndZ=0
    g16: LineSegment StartX=0 StartY=-317.5 StartZ=0 EndX=0 EndY=-338.5 EndZ=0
    g17: LineSegment StartX=0 StartY=-338.5 StartZ=0 EndX=12.5 EndY=-338.5 EndZ=0
    g18: LineSegment StartX=12.5 StartY=-338.5 StartZ=0 EndX=12.5 EndY=-317.5 EndZ=0
    g19: LineSegment StartX=12.5 StartY=-317.5 StartZ=0 EndX=0 EndY=-317.5 EndZ=0
    g20: LineSegment StartX=0 StartY=-351.5 StartZ=0 EndX=0 EndY=-372.5 EndZ=0
    g21: LineSegment StartX=0 StartY=-372.5 StartZ=0 EndX=12.5 EndY=-372.5 EndZ=0
    g22: LineSegment StartX=12.5 StartY=-372.5 StartZ=0 EndX=12.5 EndY=-351.5 EndZ=0
    g23: LineSegment StartX=12.5 StartY=-351.5 StartZ=0 EndX=0 EndY=-351.5 EndZ=0
    g24: LineSegment StartX=0 StartY=-465.5 StartZ=0 EndX=0 EndY=-486.5 EndZ=0
    g25: LineSegment StartX=0 StartY=-486.5 StartZ=0 EndX=12.5 EndY=-486.5 EndZ=0
    g26: LineSegment StartX=12.5 StartY=-486.5 StartZ=0 EndX=12.5 EndY=-465.5 EndZ=0
    g27: LineSegment StartX=12.5 StartY=-465.5 StartZ=0 EndX=0 EndY=-465.5 EndZ=0
    g28: LineSegment StartX=0 StartY=-499.5 StartZ=0 EndX=0 EndY=-520.5 EndZ=0
    g29: LineSegment StartX=0 StartY=-520.5 StartZ=0 EndX=12.5 EndY=-520.5 EndZ=0
    g30: LineSegment StartX=12.5 StartY=-520.5 StartZ=0 EndX=12.5 EndY=-499.5 EndZ=0
    g31: LineSegment StartX=12.5 StartY=-499.5 StartZ=0 EndX=0 EndY=-499.5 EndZ=0
  constraints (96):
    c: Coincident(g0,g1)
    c: Coincident(g1,g2)
    c: Coincident(g2,g3)
    c: Coincident(g3,g0)
    c: Vertical(g0)
    c: Vertical(g2)
    c: Horizontal(g1)
    c: Horizontal(g3)
    c: PointOnObject(g0,g-3)
    c: Coincident(g4,g5)
    c: Coincident(g5,g6)
    c: Coincident(g6,g7)
    c: Coincident(g7,g4)
    c: Vertical(g4)
    c: Vertical(g6)
    c: Horizontal(g5)
    c: Horizontal(g7)
    c: PointOnObject(g4,g-3)
    c: DistanceY(g0,g-1) = 22.5
    c: DistanceX(g-1,g2) = 12.5
    c: DistanceY(g0,g-1) = 43.5
    c: Equal(g1,g7)
    c: Equal(g0,g4)
    c: Coincident(g8,g9)
    c: Coincident(g9,g10)
    c: Coincident(g10,g11)
    c: Coincident(g11,g8)
    c: Vertical(g8)
    c: Vertical(g10)
    c: Horizontal(g9)
    c: Horizontal(g11)
    c: PointOnObject(g8,g-3)
    c: Coincident(g12,g13)
    c: Coincident(g13,g14)
    c: Coincident(g14,g15)
    c: Coincident(g15,g12)
    c: Vertical(g12)
    c: Vertical(g14)
    c: Horizontal(g13)
    c: Horizontal(g15)
    c: PointOnObject(g12,g-3)
    c: Coincident(g16,g17)
    c: Coincident(g17,g18)
    c: Coincident(g18,g19)
    c: Coincident(g19,g16)
    c: Vertical(g16)
    c: Vertical(g18)
    c: Horizontal(g17)
    c: Horizontal(g19)
    c: PointOnObject(g16,g-3)
    c: Coincident(g20,g21)
    c: Coincident(g21,g22)
    c: Coincident(g22,g23)
    c: Coincident(g23,g20)
    c: Vertical(g20)
    c: Vertical(g22)
    c: Horizontal(g21)
    c: Horizontal(g23)
    c: PointOnObject(g20,g-3)
    c: Coincident(g24,g25)
    c: Coincident(g25,g26)
    c: Coincident(g26,g27)
    c: Coincident(g27,g24)
    c: Vertical(g24)
    c: Vertical(g26)
    c: Horizontal(g25)
    c: Horizontal(g27)
    c: PointOnObject(g24,g-3)
    c: Coincident(g28,g29)
    c: Coincident(g29,g30)
    c: Coincident(g30,g31)
    c: Coincident(g31,g28)
    c: Vertical(g28)
    c: Vertical(g30)
    c: Horizontal(g29)
    c: Horizontal(g31)
    c: PointOnObject(g28,g-3)
    c: Equal(g5,g11)
    c: Equal(g4,g8)
    c: Equal(g9,g15)
    c: Equal(g8,g12)
    c: Equal(g13,g19)
    c: Equal(g12,g16)
    c: Equal(g17,g23)
    c: Equal(g16,g20)
    c: Equal(g21,g27)
    c: Equal(g25,g31)
    c: Equal(g20,g24)
    c: Equal(g24,g28)
    c: DistanceY(g4,g0) = 13
    c: DistanceY(g12,g8) = 13
    c: DistanceY(g20,g16) = 13
    c: DistanceY(g28,g24) = 13
    c: DistanceY(g8,g4) = 95
    c: DistanceY(g16,g12) = 90
    c: DistanceY(g24,g20) = 93
FEATURE [PartDesign::Pocket] Pocket014
  BaseFeature = -> Pocket009
  Direction = (0,0,-1)
  Length = 111
  Length2 = 5
  Placement = pos=(0,0,0) rot=(1,0,0;1.5708rad)
  Profile = -> Sketch019
  ReferenceAxis = -> Sketch019 [N_Axis]
  Refine = true
  Reversed = true
  Suppressed = false
  Type = 1
FEATURE [PartDesign::Fillet] Fillet
  Base = -> Pocket014 [Edge14,Edge91,Edge87,Edge83,Edge79]
  BaseFeature = -> Pocket014
  Placement = pos=(0,0,0) rot=(1,0,0;1.5708rad)
  Radius = 5
  Refine = true
  SupportTransform = false
  Suppressed = false
  UseAllEdges = false
FEATURE [PartDesign::Chamfer] Chamfer
  Angle = 45
  Base = -> Fillet [Edge171,Edge176,Edge194,Edge200,Edge218,Edge224,Edge242,Edge16]
  BaseFeature = -> Fillet
  ChamferType = 0
  FlipDirection = false
  Placement = pos=(0,0,0) rot=(1,0,0;1.5708rad)
  Refine = true
  Size = 3
  Size2 = 1
  SupportTransform = false
  Suppressed = false
  UseAllEdges = false
FEATURE [PartDesign::Body] Body004  label="Case"
  AllowCompound = false
  Group = -> [Sketch014,Pad006,Sketch015,Pocket008,Sketch016,Pocket009,Sketch019,Pocket014,Fillet,Chamfer]
  Origin = -> Origin004
  Placement = pos=(0,43,0) rot=(0,0,1;0rad)
  Tip = -> Chamfer
COMPONENT P5 — recipe-attached ("CaseInterior", modeled in this document).
Construction recipe (the document's own serialized feature program — sketch geometry with constraints, then the solid features built on it; lengths are millimeters unless a unit is written):

FEATURE [Sketcher::SketchObject] Sketch017
  ArcFitTolerance = 1e-06
  AttachmentSupport = -> [XY_Plane005]
  FullyConstrained = false
  MakeInternals = false
  MapMode = 5
  sketch-geometry (4):
    g0: LineSegment StartX=118.624 StartY=41.6118 StartZ=0 EndX=10.0253 EndY=41.6118 EndZ=0
    g1: LineSegment StartX=10.0253 StartY=41.6118 StartZ=0 EndX=10.0253 EndY=-59.5336 EndZ=0
    g2: LineSegment StartX=10.0253 StartY=-59.5336 StartZ=0 EndX=118.624 EndY=-59.5336 EndZ=0
    g3: LineSegment StartX=118.624 StartY=-59.5336 StartZ=0 EndX=118.624 EndY=41.6118 EndZ=0
  constraints (8):
    c: Coincident(g0,g1)
    c: Coincident(g1,g2)
    c: Coincident(g2,g3)
    c: Coincident(g3,g0)
    c: Horizontal(g0)
    c: Horizontal(g2)
    c: Vertical(g1)
    c: Vertical(g3)
FEATURE [PartDesign::Pad] Pad007
  Direction = (0,0,1)
  Length = 170
  Length2 = 10
  Profile = -> Sketch017
  ReferenceAxis = -> Sketch017 [N_Axis]
  Refine = true
  Suppressed = false
  Type = 0
FEATURE [Sketcher::SketchObject] Sketch018
  ArcFitTolerance = 1e-06
  AttachmentSupport = -> [XY_Plane005]
  ExternalGeometry = -> [Pad007]
  FullyConstrained = true
  MakeInternals = false
  MapMode = 5
  sketch-geometry (1):
    g0: Circle CenterX=0.01 CenterY=-7.49 CenterZ=0 NormalX=0 NormalY=0 NormalZ=1 AngleXU=0 Radius=35
  constraints (3):
    c: Diameter(g0) = 70
    c: DistanceX(g-1,g0) = 0.01
    c: DistanceY(g0,g-1) = 7.49
FEATURE [PartDesign::Pocket] Pocket011
  BaseFeature = -> Pad007
  Direction = (0,0,-1)
  Length = 5
  Length2 = 5
  Profile = -> Sketch018
  ReferenceAxis = -> Sketch018 [N_Axis]
  Refine = true
  Suppressed = false
  Type = 1
FEATURE [PartDesign::Pocket] Pocket012
  BaseFeature = -> Pocket011
  Direction = (0,0,-1)
  Length = 5
  Length2 = 5
  Midplane = true
  Profile = -> Sketch018
  ReferenceAxis = -> Sketch018 [N_Axis]
  Refine = true
  Suppressed = false
  Type = 1
FEATURE [PartDesign::Body] Body005  label="CaseInterior"
  AllowCompound = false
  Group = -> [Sketch017,Pad007,Sketch018,Pocket011,Pocket012]
  Origin = -> Origin005
  Placement = pos=(0,0,67) rot=(0,0,1;0rad)
  Tip = -> Pocket012
COMPONENT P6 — recipe-attached ("Supapa", modeled in this document).
Construction recipe (the document's own serialized feature program — sketch geometry with constraints, then the solid features built on it; lengths are millimeters unless a unit is written):

FEATURE [Sketcher::SketchObject] Sketch020
  ArcFitTolerance = 1e-06
  AttachmentSupport = -> [XY_Plane007]
  FullyConstrained = false
  MakeInternals = false
  MapMode = 5
  sketch-geometry (4):
    g0: LineSegment StartX=0 StartY=20.4996 StartZ=0 EndX=0 EndY=-0.500933 EndZ=0
    g1: LineSegment StartX=0 StartY=-0.500933 StartZ=0 EndX=12.4997 EndY=-0.500933 EndZ=0
    g2: LineSegment StartX=12.4997 StartY=-0.500933 StartZ=0 EndX=12.4997 EndY=20.4996 EndZ=0
    g3: LineSegment StartX=12.4997 StartY=20.4996 StartZ=0 EndX=0 EndY=20.4996 EndZ=0
  constraints (9):
    c: Coincident(g0,g1)
    c: Coincident(g1,g2)
    c: Coincident(g2,g3)
    c: Coincident(g3,g0)
    c: Vertical(g0)
    c: Vertical(g2)
    c: Horizontal(g1)
    c: Horizontal(g3)
    c: PointOnObject(g0,g-2)
FEATURE [PartDesign::Pad] Pad008
  Direction = (0,0,1)
  Length = 8
  Length2 = 10
  Profile = -> Sketch020
  ReferenceAxis = -> Sketch020 [N_Axis]
  Refine = true
  Suppressed = false
  Type = 0
FEATURE [Sketcher::SketchObject] Sketch021
  ArcFitTolerance = 1e-06
  AttachmentSupport = -> [Pad008]
  ExternalGeometry = -> [Pad008]
  FullyConstrained = false
  MakeInternals = false
  MapMode = 5
  Placement = pos=(0,0,8) rot=(0,0,1;0rad)
  sketch-geometry (1):
    g0: Circle CenterX=6.35 CenterY=9.99907 CenterZ=0 NormalX=0 NormalY=0 NormalZ=1 AngleXU=0 Radius=1.98528
  constraints (2):
    c: Distance(g0,g-4) = 10.5
    c: DistanceX(g-1,g0) = 6.35
FEATURE [PartDesign::Pad] Pad009
  BaseFeature = -> Pad008
  Direction = (0,0,1)
  Length = 20
  Length2 = 10
  Profile = -> Sketch021
  ReferenceAxis = -> Sketch021 [N_Axis]
  Refine = true
  Suppressed = false
  Type = 0
FEATURE [PartDesign::Body] Body008  label="Supapa"
  AllowCompound = false
  Group = -> [Sketch020,Pad008,Sketch021,Pad009]
  Origin = -> Origin007
  Placement = pos=(0,0,236) rot=(0,0,1;0rad)
  Tip = -> Pad009
PROVENANCE & LICENSES
A FreeCAD (.FCStd) document from a public repository crawl; recipes are the document's own serialized feature recipes (and, for linked parts, companion documents' recipes).
License: as declared in the source repository (recorded in the dataset sidecar).
